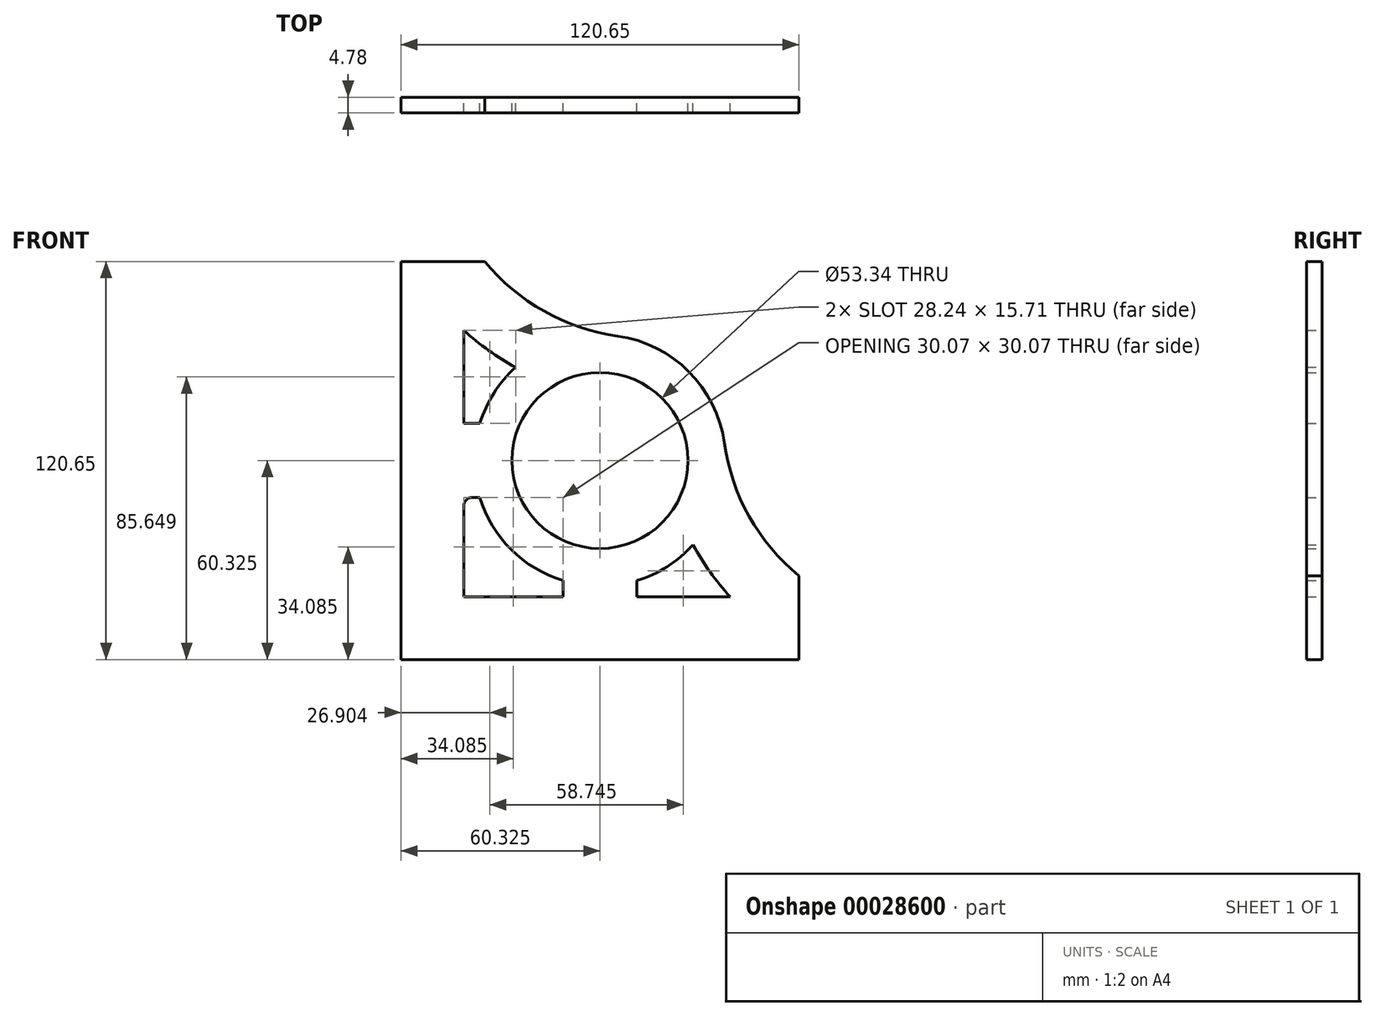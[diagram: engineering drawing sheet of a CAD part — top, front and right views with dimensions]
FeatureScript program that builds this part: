
annotation { "Feature Type Name" : "Feature", "Feature Type Description" : "" }
export const myFeature = defineFeature(function(context is Context, id is Id, definition is map)
    precondition{}
    {
        {
            var Q0;
            Q0=qCreatedBy(makeId("Front.planeOp"),FACE);
            var sketch = newSketch(context, id + "F0", { "sketchPlane" : qUnion([Q0])});
            skLineSegment(sketch, "E0.bottom", {"start": v(0, 0) * mm, "end": v(120.65, 0) * mm});
            skLineSegment(sketch, "E0.top", {"start": v(0, 120.65) * mm, "end": v(25.4, 120.65) * mm});
            skLineSegment(sketch, "E0.left", {"start": v(0, 0) * mm, "end": v(0, 120.65) * mm});
            skLineSegment(sketch, "E0.right", {"start": v(120.65, 0) * mm, "end": v(120.65, 25.4) * mm});
            skArc(sketch, "E1", {"start": v(34.76, 88.57) * mm, "mid": v(28.18, 80.78) * mm, "end": v(23.91, 71.53) * mm});
            skArc(sketch, "E2", {"start": v(25.4, 120.65) * mm, "mid": v(43.4, 105.57) * mm, "end": v(65.64, 98.05) * mm});
            skArc(sketch, "E3", {"start": v(98.05, 65.64) * mm, "mid": v(105.57, 43.4) * mm, "end": v(120.65, 25.4) * mm});
            skLineSegment(sketch, "E4.0", {"start": v(19.05, 19.05) * mm, "end": v(19.05, 49.12) * mm});
            skLineSegment(sketch, "E4.1", {"start": v(19.05, 19.05) * mm, "end": v(49.12, 19.05) * mm});
            skArc(sketch, "E5.0", {"start": v(19.05, 99.77) * mm, "mid": v(26.58, 93.7) * mm, "end": v(34.76, 88.57) * mm});
            skArc(sketch, "E6.0", {"start": v(88.57, 34.76) * mm, "mid": v(93.7, 26.58) * mm, "end": v(99.77, 19.05) * mm});
            skArc(sketch, "E7.trimOffspring", {"start": v(98.05, 65.64) * mm, "mid": v(87.27, 87.27) * mm, "end": v(65.64, 98.05) * mm});
            skLineSegment(sketch, "E8.0", {"start": v(19.05, 49.12) * mm, "end": v(23.91, 49.12) * mm});
            skLineSegment(sketch, "E9.0", {"start": v(19.05, 71.53) * mm, "end": v(23.91, 71.53) * mm});
            skLineSegment(sketch, "E10.0", {"start": v(71.53, 19.05) * mm, "end": v(71.53, 23.91) * mm});
            skLineSegment(sketch, "E11.0", {"start": v(49.12, 19.05) * mm, "end": v(49.12, 23.91) * mm});
            skPoint(sketch, "E12.start.orphan", {"position": v(19.05, 60.33) * mm});
            skArc(sketch, "E13.trimOffspring", {"start": v(23.91, 49.12) * mm, "mid": v(33.38, 33.38) * mm, "end": v(49.12, 23.91) * mm});
            skLineSegment(sketch, "E14.trimOffspring", {"start": v(19.05, 71.53) * mm, "end": v(19.05, 99.77) * mm});
            skArc(sketch, "E15.trimOffspring", {"start": v(71.53, 23.91) * mm, "mid": v(80.78, 28.18) * mm, "end": v(88.57, 34.76) * mm});
            skPoint(sketch, "E16.start.orphan", {"position": v(60.33, 19.05) * mm});
            skLineSegment(sketch, "E17.trimOffspring", {"start": v(71.53, 19.05) * mm, "end": v(99.77, 19.05) * mm});
            skCircle(sketch, "E18", {"center": v(60.33, 60.33) * mm, "radius": 26.67 * mm});
            skSolve(sketch);
        }
        {
            var Q0;
            Q0=makeQuery(id+"F0.imprint","IMPRINT",FACE,{"disambiguationData":[TD([[makeQuery(id+"F0.imprint","IMPRINT",EDGE,{"derivedFrom":sQuery(id+"F0.wireOp",EDGE,"E0.bottom")}),1.0]])]});
            extrude(context, id + "F1", {"entities" : qUnion([Q0]), "depth" : 4.78 * mm});
        }
        {
            var Q0;
            Q0=makeQuery(id+"F1.opExtrude","SWEPT_EDGE",EDGE,{"disambiguationData":[OSD([sQuery(id+"F0.wireOp",EDGE,"E4.0"),sQuery(id+"F0.wireOp",EDGE,"E8.0")])]});
            fillet(context, id + "F2", {"entities" : qUnion([Q0]), "radius" : 2.54 * mm, "tangentPropagation" : true, "allowEdgeOverflow" : false});
        }
    });
